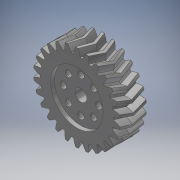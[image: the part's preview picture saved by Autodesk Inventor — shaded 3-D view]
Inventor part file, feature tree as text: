
AUTODESK INVENTOR PART (.ipt)
format: ipt  version: 2019 (Build 230136000, 136)  size: 1,241,088 bytes
history: native  units: mm (DEFAULTED — no unit token found)
features: sketch x6, extrude x3, plane x3, other x3, mirror x2, hole x2, chamfer x1
ambient origin geometry x8: Origin, YZ Plane, XZ Plane, XY Plane, X Axis, Y Axis, Z Axis, Center Point
bodies: Solid1 (feature_tree)
feature tree (20):
  extrude  "Extrusion1"  Depth=5.0mm TaperAngle=0.0deg
  plane  "Work Plane2"
  plane  "Work Plane8"
  plane  "Work Plane9"
  other  "Spur Gear"
  mirror  "Mirror1"
  extrude  "Extrusion2"  Depth=10.0mm TaperAngle=0.0deg
  hole  "Hole1"  [1 undecoded]
  hole  "Hole2"  [1 undecoded]
  extrude  "Extrusion3"  Depth=31.29mm
  chamfer  "Chamfer1"  [1 undecoded]
  mirror  "Mirror2"
  sketch  "Sketch1"  dims[d0=32.949264mm d1=5.0mm d2=0.0mm]
  sketch  "Sketch2"  dims[d3=30.699623mm d4=10.0mm d5=0.0mm]
  other  "Srf1"
  sketch  "Sketch3"  dims[d16=31.29mm d17=0.0mm d34=1.208305mm]
  sketch  "Sketch4"  dims[d39=0.0mm d41=0.0mm]
  sketch  "Sketch5"  dims[d43=31.29mm d46=31.29mm d47=0.0mm d48=0.0mm]
  sketch  "Sketch6"  dims[d49=18.0mm d50=5.0mm d51=0.0mm d52=13.5mm d53=80.0mm d55=360.0deg d57=2.5mm d58=6.0mm d59=4.0mm d60=3.0mm d61=90.0deg d62=8.0mm d63=0.0mm d64=4.5mm d65=6.0mm d66=4.0mm d67=3.0mm d68=90.0deg d69=8.0mm d70=0.0mm d71=20.0mm d72=1.55mm d73=0.0mm d74=1.5mm d75=4.0mm d76=45.0deg]
  other  "Pitch Diameter"
note: 3 required parameter values undecoded (feature->parameter linkage not recoverable at this tier; creation-order binding heuristic only, values carry confidence <= 0.55)
